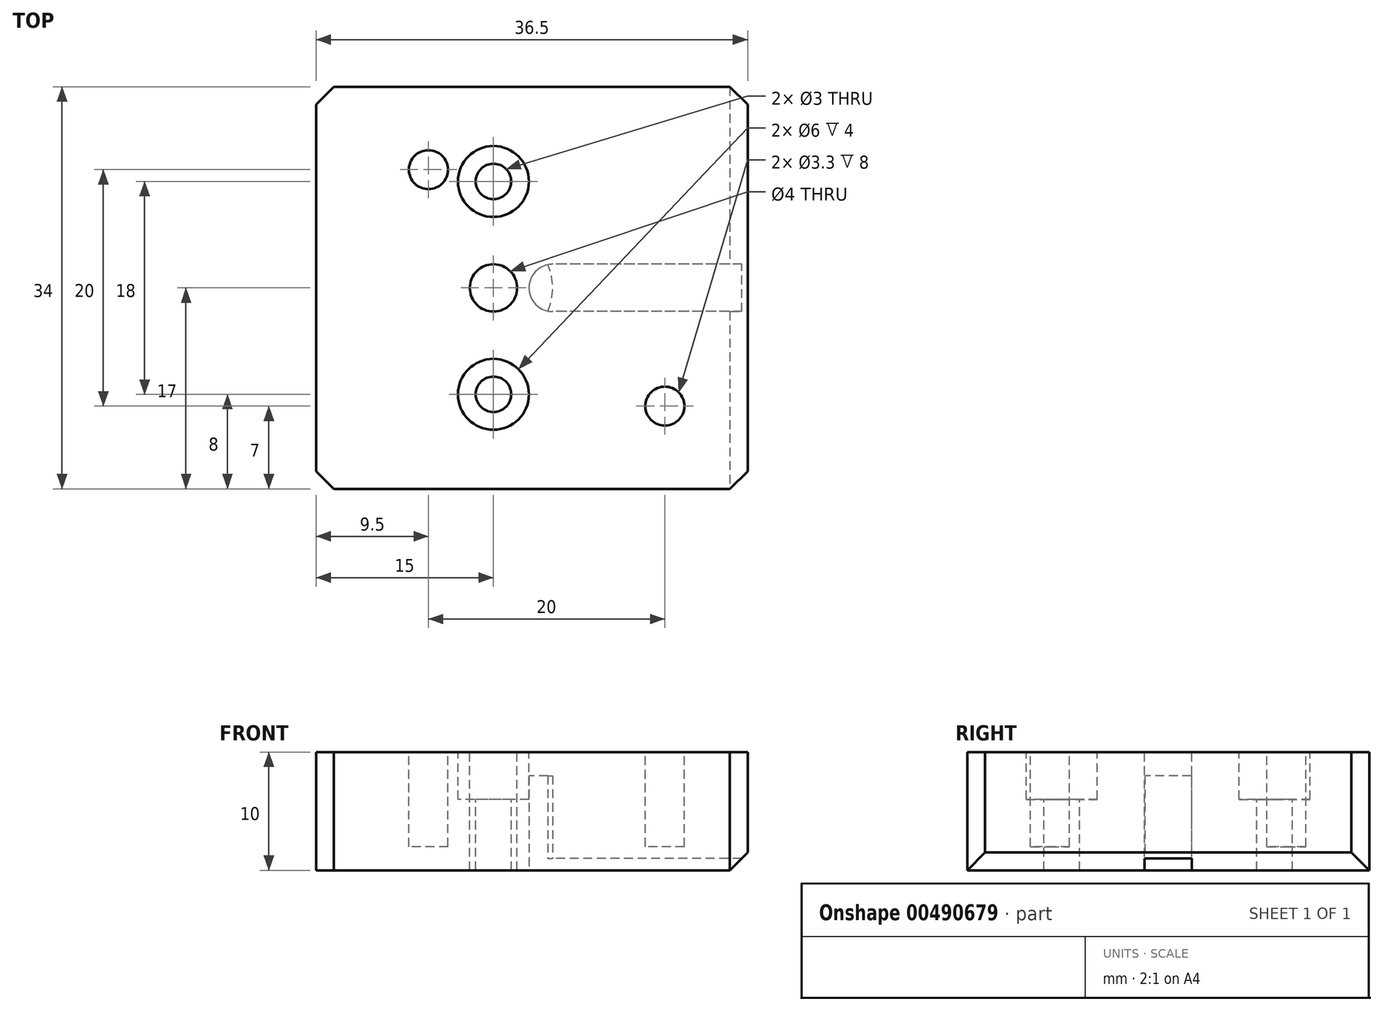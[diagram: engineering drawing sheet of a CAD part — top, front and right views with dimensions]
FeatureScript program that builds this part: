
annotation { "Feature Type Name" : "Feature", "Feature Type Description" : "" }
export const myFeature = defineFeature(function(context is Context, id is Id, definition is map)
    precondition{}
    {
        {
            var Q0;
            Q0=qCreatedBy(makeId("Top.planeOp"),FACE);
            var sketch = newSketch(context, id + "F0", { "sketchPlane" : qUnion([Q0])});
            skLineSegment(sketch, "E0.bottom", {"start": v(0, 0) * mm, "end": v(30, 0) * mm});
            skLineSegment(sketch, "E0.top", {"start": v(0, -30) * mm, "end": v(30, -30) * mm});
            skLineSegment(sketch, "E0.left", {"start": v(0, 0) * mm, "end": v(0, -30) * mm});
            skLineSegment(sketch, "E0.right", {"start": v(30, 0) * mm, "end": v(30, -30) * mm});
            skLineSegment(sketch, "E1", {"start": v(0, -15) * mm, "end": v(30, -15) * mm, "construction": true});
            skCircle(sketch, "E2", {"center": v(15, -15) * mm, "radius": 2 * mm});
            skLineSegment(sketch, "E3", {"start": v(0, -5) * mm, "end": v(9.5, -5) * mm, "construction": true});
            skLineSegment(sketch, "E4", {"start": v(9.5, -5) * mm, "end": v(9.5, 0) * mm, "construction": true});
            skCircle(sketch, "E5", {"center": v(9.5, -5) * mm, "radius": 1.65 * mm});
            skCircle(sketch, "E6.0.1.0", {"center": v(9.5, -25) * mm, "radius": 1.65 * mm, "construction": true});
            skLineSegment(sketch, "E6.direction2", {"start": v(9.5, -5) * mm, "end": v(9.5, -25) * mm, "construction": true});
            skLineSegment(sketch, "E7", {"start": v(15, -30) * mm, "end": v(15, 0) * mm, "construction": true});
            skCircle(sketch, "E8", {"center": v(15, -6) * mm, "radius": 1.5 * mm});
            skCircle(sketch, "E9", {"center": v(15, -24) * mm, "radius": 1.5 * mm});
            skCircle(sketch, "E10", {"center": v(15, -6) * mm, "radius": 3 * mm});
            skCircle(sketch, "E11", {"center": v(15, -24) * mm, "radius": 3 * mm});
            skCircle(sketch, "E12", {"center": v(6, -15) * mm, "radius": 1.5 * mm});
            skCircle(sketch, "E13", {"center": v(6, -15) * mm, "radius": 3 * mm});
            skCircle(sketch, "E14", {"center": v(24, -15) * mm, "radius": 3 * mm});
            skCircle(sketch, "E15", {"center": v(24, -15) * mm, "radius": 1.5 * mm});
            skSolve(sketch);
        }
        {
            var Q0;
            Q0=makeQuery(id+"F0.imprint","IMPRINT",FACE,{"disambiguationData":[TD([[makeQuery(id+"F0.imprint","IMPRINT",EDGE,{"derivedFrom":sQuery(id+"F0.wireOp",EDGE,"E0.bottom")}),-1.0]])]});
            var Q1;
            Q1=makeQuery(id+"F0.imprint","IMPRINT",FACE,{"disambiguationData":[TD([[makeQuery(id+"F0.imprint","IMPRINT",EDGE,{"derivedFrom":sQuery(id+"F0.wireOp",EDGE,"E2")}),1.0]])]});
            var Q2;
            Q2=makeQuery(id+"F0.imprint","IMPRINT",FACE,{"disambiguationData":[TD([[makeQuery(id+"F0.imprint","IMPRINT",EDGE,{"derivedFrom":sQuery(id+"F0.wireOp",EDGE,"E8")}),-1.0]])]});
            var Q3;
            Q3=makeQuery(id+"F0.imprint","IMPRINT",FACE,{"disambiguationData":[TD([[makeQuery(id+"F0.imprint","IMPRINT",EDGE,{"derivedFrom":sQuery(id+"F0.wireOp",EDGE,"E9")}),-1.0]])]});
            var Q4;
            Q4=makeQuery(id+"F0.imprint","IMPRINT",FACE,{"disambiguationData":[TD([[makeQuery(id+"F0.imprint","IMPRINT",EDGE,{"derivedFrom":sQuery(id+"F0.wireOp",EDGE,"E5")}),1.0]])]});
            var Q5;
            Q5=makeQuery(id+"F0.imprint","IMPRINT",FACE,{"disambiguationData":[TD([[makeQuery(id+"F0.imprint","IMPRINT",EDGE,{"derivedFrom":sQuery(id+"F0.wireOp",EDGE,"E6.0.1.0")}),1.0]])]});
            var Q6;
            Q6=makeQuery(id+"F0.imprint","IMPRINT",FACE,{"disambiguationData":[TD([[makeQuery(id+"F0.imprint","IMPRINT",EDGE,{"derivedFrom":sQuery(id+"F0.wireOp",EDGE,"E14")}),1.0]])]});
            var Q7;
            Q7=makeQuery(id+"F0.imprint","IMPRINT",FACE,{"disambiguationData":[TD([[makeQuery(id+"F0.imprint","IMPRINT",EDGE,{"derivedFrom":sQuery(id+"F0.wireOp",EDGE,"E12")}),-1.0]])]});
            var Q8;
            Q8=makeQuery(id+"F0.imprint","IMPRINT",FACE,{"disambiguationData":[TD([[makeQuery(id+"F0.imprint","IMPRINT",EDGE,{"derivedFrom":sQuery(id+"F0.wireOp",EDGE,"E12")}),1.0]])]});
            var Q9;
            Q9=makeQuery(id+"F0.imprint","IMPRINT",FACE,{"disambiguationData":[TD([[makeQuery(id+"F0.imprint","IMPRINT",EDGE,{"derivedFrom":sQuery(id+"F0.wireOp",EDGE,"E15")}),1.0]])]});
            extrude(context, id + "F1", {"entities" : qUnion([Q0, Q1, Q2, Q3, Q4, Q5, Q6, Q7, Q8, Q9]), "oppositeDirection" : true, "depth" : 10 * mm, "offsetDistance" : 25 * mm});
        }
        {
            var Q0;
            Q0=makeQuery(id+"F0.imprint","IMPRINT",FACE,{"disambiguationData":[TD([[makeQuery(id+"F0.imprint","IMPRINT",EDGE,{"derivedFrom":sQuery(id+"F0.wireOp",EDGE,"CrWIfdQ6-x99r-vkrS-wa22-O8fHmD59tpvO")}),1.0]])]});
            var Q1;
            Q1=makeQuery(id+"F0.imprint","IMPRINT",FACE,{"disambiguationData":[TD([[makeQuery(id+"F0.imprint","IMPRINT",EDGE,{"derivedFrom":sQuery(id+"F0.wireOp",EDGE,"E2")}),1.0]])]});
            extrude(context, id + "F2", {"entities" : qUnion([Q0, Q1]), "operationType" : NewBodyOperationType.REMOVE, "oppositeDirection" : true, "depth" : 12 * mm, "offsetDistance" : 25 * mm});
        }
        {
            var Q0;
            Q0=makeQuery(id+"F0.imprint","IMPRINT",FACE,{"disambiguationData":[TD([[makeQuery(id+"F0.imprint","IMPRINT",EDGE,{"derivedFrom":sQuery(id+"F0.wireOp",EDGE,"E9")}),-1.0]])]});
            var Q1;
            Q1=makeQuery(id+"F0.imprint","IMPRINT",FACE,{"disambiguationData":[TD([[makeQuery(id+"F0.imprint","IMPRINT",EDGE,{"derivedFrom":sQuery(id+"F0.wireOp",EDGE,"E8")}),-1.0]])]});
            extrude(context, id + "F3", {"entities" : qUnion([Q0, Q1]), "operationType" : NewBodyOperationType.REMOVE, "oppositeDirection" : true, "depth" : 4 * mm, "offsetDistance" : 25 * mm});
        }
        {
            var Q0;
            Q0=makeQuery(id+"F1.opExtrude","CAP_FACE",FACE,{"disambiguationData":[OSD([sQuery(id+"F0.wireOp",EDGE,"E0.bottom"),sQuery(id+"F0.wireOp",EDGE,"E0.top"),sQuery(id+"F0.wireOp",EDGE,"E0.left"),sQuery(id+"F0.wireOp",EDGE,"E0.right"),sQuery(id+"F0.wireOp",EDGE,"E8"),sQuery(id+"F0.wireOp",EDGE,"E9")])],"isStart":false});
            var sketch = newSketch(context, id + "F4", { "sketchPlane" : qUnion([Q0])});
            skCircle(sketch, "E16", {"center": v(15, 15) * mm, "radius": 5 * mm});
            skLineSegment(sketch, "E17", {"start": v(30, 15) * mm, "end": v(20, 15) * mm, "construction": true});
            skArc(sketch, "E18.0.startCap", {"start": v(30, 17) * mm, "mid": v(32, 15) * mm, "end": v(30, 13) * mm});
            skArc(sketch, "E18.0.endCap", {"start": v(20, 13) * mm, "mid": v(18, 15) * mm, "end": v(20, 17) * mm});
            skLineSegment(sketch, "E18.0.left", {"start": v(30, 13) * mm, "end": v(20, 13) * mm});
            skLineSegment(sketch, "E18.0.right", {"start": v(30, 17) * mm, "end": v(20, 17) * mm});
            skLineSegment(sketch, "E19", {"start": v(3.5, 0) * mm, "end": v(3.5, 3.5) * mm, "construction": true});
            skLineSegment(sketch, "E20", {"start": v(3.5, 3.5) * mm, "end": v(0, 3.5) * mm, "construction": true});
            skCircle(sketch, "E21", {"center": v(3.5, 3.5) * mm, "radius": 1.25 * mm});
            skCircle(sketch, "E22", {"center": v(3.5, 3.5) * mm, "radius": 2.5 * mm});
            skCircle(sketch, "E23.0.1.0", {"center": v(3.5, 26.5) * mm, "radius": 1.25 * mm});
            skCircle(sketch, "E23.0.1.1", {"center": v(3.5, 26.5) * mm, "radius": 2.5 * mm});
            skCircle(sketch, "E23.1.0.0", {"center": v(26.5, 3.5) * mm, "radius": 1.25 * mm});
            skCircle(sketch, "E23.1.0.1", {"center": v(26.5, 3.5) * mm, "radius": 2.5 * mm});
            skCircle(sketch, "E23.1.1.0", {"center": v(26.5, 26.5) * mm, "radius": 1.25 * mm});
            skCircle(sketch, "E23.1.1.1", {"center": v(26.5, 26.5) * mm, "radius": 2.5 * mm});
            skLineSegment(sketch, "E23.direction1", {"start": v(3.5, 3.5) * mm, "end": v(26.5, 3.5) * mm, "construction": true});
            skLineSegment(sketch, "E23.direction2", {"start": v(3.5, 3.5) * mm, "end": v(3.5, 26.5) * mm, "construction": true});
            skSolve(sketch);
        }
        {
            var Q0;
            Q0=makeQuery(id+"F4.imprint","IMPRINT",FACE,{"disambiguationData":[TD([[makeQuery(id+"F4.imprint","IMPRINT",EDGE,{"derivedFrom":sQuery(id+"F4.wireOp",EDGE,"E16")}),1.0]])]});
            var Q1;
            {var subQ0=sQuery(id+"F4.wireOp",EDGE,"E18.0.endCap");var subQ1=sQuery(id+"F4.wireOp",EDGE,"E16");var subQ2=makeQuery(id+"F4.imprint","INTERSECT",VERTEX,{"disambiguationData":[OD(0.0)],"derivedFrom":[subQ1,subQ0]});Q1=makeQuery(id+"F4.imprint","IMPRINT",FACE,{"disambiguationData":[TD([[makeQuery(id+"F4.imprint","IMPRINT",EDGE,{"disambiguationData":[TD([[subQ2,1.0]])],"derivedFrom":subQ1}),1.0]])]});}
            extrude(context, id + "F5", {"entities" : qUnion([Q0, Q1]), "operationType" : NewBodyOperationType.REMOVE, "oppositeDirection" : true, "depth" : 8 * mm, "offsetDistance" : 25 * mm});
        }
        {
            var Q0;
            {var subQ4=sQuery(id+"F4.wireOp",EDGE,"E18.0.left");Q0=makeQuery(id+"F4.imprint","IMPRINT",FACE,{"disambiguationData":[TD([[makeQuery(id+"F4.imprint","IMPRINT",EDGE,{"derivedFrom":subQ4}),-1.0]])]});}
            extrude(context, id + "F6", {"entities" : qUnion([Q0]), "operationType" : NewBodyOperationType.REMOVE, "oppositeDirection" : true, "depth" : 1 * mm, "offsetDistance" : 25 * mm});
        }
        {
            var Q0;
            Q0=makeQuery(id+"F1.opExtrude","SWEPT_FACE",FACE,{"disambiguationData":[OSD([sQuery(id+"F0.wireOp",EDGE,"E0.right")])]});
            extrude(context, id + "F7", {"entities" : qUnion([Q0]), "operationType" : NewBodyOperationType.ADD, "depth" : 4.5 * mm, "offsetDistance" : 25 * mm});
        }
        {
            var Q0;
            {var subQ0=sQuery(id+"F0.wireOp",EDGE,"E0.bottom");Q0=makeQuery(id+"F7.boolean.opBoolean","MERGE",FACE,{"derivedFrom":[makeQuery(id+"F1.opExtrude","SWEPT_FACE",FACE,{"disambiguationData":[OSD([subQ0])]}),makeQuery(id+"F7.opExtrude","SWEPT_FACE",FACE,{"disambiguationData":[OSD([subQ0,sQuery(id+"F0.wireOp",EDGE,"E0.right")])]})]});}
            extrude(context, id + "F8", {"entities" : qUnion([Q0]), "operationType" : NewBodyOperationType.ADD, "depth" : 2 * mm, "offsetDistance" : 25 * mm});
        }
        {
            var Q0;
            {var subQ0=sQuery(id+"F0.wireOp",EDGE,"E0.top");Q0=makeQuery(id+"F7.boolean.opBoolean","MERGE",FACE,{"derivedFrom":[makeQuery(id+"F1.opExtrude","SWEPT_FACE",FACE,{"disambiguationData":[OSD([subQ0])]}),makeQuery(id+"F7.opExtrude","SWEPT_FACE",FACE,{"disambiguationData":[OSD([subQ0,sQuery(id+"F0.wireOp",EDGE,"E0.right")])]})]});}
            extrude(context, id + "F9", {"entities" : qUnion([Q0]), "operationType" : NewBodyOperationType.ADD, "depth" : 2 * mm, "offsetDistance" : 25 * mm});
        }
        {
            var Q0;
            {var subQ0=sQuery(id+"F0.wireOp",EDGE,"E0.right");var subQ1=sQuery(id+"F0.wireOp",EDGE,"E0.top");var subQ2=sQuery(id+"F0.wireOp",EDGE,"E0.bottom");Q0=makeQuery(id+"F9.boolean.opBoolean","MERGE",FACE,{"derivedFrom":[makeQuery(id+"F8.boolean.opBoolean","MERGE",FACE,{"derivedFrom":[makeQuery(id+"F7.opExtrude","CAP_FACE",FACE,{"disambiguationData":[OSD([subQ0])],"isStart":false}),makeQuery(id+"F8.opExtrude","SWEPT_FACE",FACE,{"disambiguationData":[OSD([subQ2,subQ0]),TDD([makeQuery(id+"F7.opExtrude","CAP_EDGE",EDGE,{"disambiguationData":[OSD([subQ2,subQ0])],"isStart":false})])]})]}),makeQuery(id+"F9.opExtrude","SWEPT_FACE",FACE,{"disambiguationData":[OSD([subQ1,subQ0]),TDD([makeQuery(id+"F7.opExtrude","CAP_EDGE",EDGE,{"disambiguationData":[OSD([subQ1,subQ0])],"isStart":false})])]})]});}
            extrude(context, id + "F10", {"entities" : qUnion([Q0]), "operationType" : NewBodyOperationType.ADD, "depth" : 2 * mm, "offsetDistance" : 25 * mm});
        }
        {
            var Q0;
            Q0=makeQuery(id+"F1.opExtrude","SWEPT_EDGE",EDGE,{"disambiguationData":[OSD([sQuery(id+"F0.wireOp",EDGE,"E0.top"),sQuery(id+"F0.wireOp",EDGE,"E0.right")])]});
            var Q1;
            Q1=makeQuery(id+"F1.opExtrude","SWEPT_EDGE",EDGE,{"disambiguationData":[OSD([sQuery(id+"F0.wireOp",EDGE,"E0.top"),sQuery(id+"F0.wireOp",EDGE,"E0.left")])]});
            var Q2;
            Q2=makeQuery(id+"F1.opExtrude","SWEPT_EDGE",EDGE,{"disambiguationData":[OSD([sQuery(id+"F0.wireOp",EDGE,"E0.bottom"),sQuery(id+"F0.wireOp",EDGE,"E0.left")])]});
            var Q3;
            Q3=makeQuery(id+"F1.opExtrude","SWEPT_EDGE",EDGE,{"disambiguationData":[OSD([sQuery(id+"F0.wireOp",EDGE,"E0.bottom"),sQuery(id+"F0.wireOp",EDGE,"E0.right")])]});
            var Q4;
            Q4=makeQuery(id+"F7.boolean.opBoolean","COPY",EDGE,{"derivedFrom":makeQuery(id+"F7.opExtrude","CAP_EDGE",EDGE,{"disambiguationData":[OSD([sQuery(id+"F0.wireOp",EDGE,"E0.top"),sQuery(id+"F0.wireOp",EDGE,"E0.right")])],"isStart":false})});
            var Q5;
            Q5=makeQuery(id+"F7.boolean.opBoolean","COPY",EDGE,{"derivedFrom":makeQuery(id+"F7.opExtrude","CAP_EDGE",EDGE,{"disambiguationData":[OSD([sQuery(id+"F0.wireOp",EDGE,"E0.bottom"),sQuery(id+"F0.wireOp",EDGE,"E0.right")])],"isStart":false})});
            var Q6;
            Q6=makeQuery(id+"F7.opExtrude","CAP_EDGE",EDGE,{"disambiguationData":[OSD([sQuery(id+"F0.wireOp",EDGE,"E0.top"),sQuery(id+"F0.wireOp",EDGE,"E0.right")])],"isStart":false});
            var Q7;
            Q7=makeQuery(id+"F7.opExtrude","CAP_EDGE",EDGE,{"disambiguationData":[OSD([sQuery(id+"F0.wireOp",EDGE,"E0.bottom"),sQuery(id+"F0.wireOp",EDGE,"E0.right")])],"isStart":false});
            var Q8;
            Q8=makeQuery(id+"F9.opExtrude","CAP_EDGE",EDGE,{"disambiguationData":[OSD([sQuery(id+"F0.wireOp",EDGE,"E0.top"),sQuery(id+"F0.wireOp",EDGE,"E0.left")])],"isStart":false});
            var Q9;
            Q9=makeQuery(id+"F8.opExtrude","CAP_EDGE",EDGE,{"disambiguationData":[OSD([sQuery(id+"F0.wireOp",EDGE,"E0.bottom"),sQuery(id+"F0.wireOp",EDGE,"E0.left")])],"isStart":false});
            var Q10;
            {var subQ0=sQuery(id+"F0.wireOp",EDGE,"E0.right");var subQ1=sQuery(id+"F0.wireOp",EDGE,"E0.top");Q10=makeQuery(id+"F9.opExtrude","CAP_EDGE",EDGE,{"disambiguationData":[OSD([subQ1,subQ0]),TDD([makeQuery(id+"F7.opExtrude","CAP_EDGE",EDGE,{"disambiguationData":[OSD([subQ1,subQ0])],"isStart":false})])],"isStart":false});}
            var Q11;
            {var subQ0=sQuery(id+"F0.wireOp",EDGE,"E0.right");var subQ1=sQuery(id+"F0.wireOp",EDGE,"E0.bottom");Q11=makeQuery(id+"F8.opExtrude","CAP_EDGE",EDGE,{"disambiguationData":[OSD([subQ1,subQ0]),TDD([makeQuery(id+"F7.opExtrude","CAP_EDGE",EDGE,{"disambiguationData":[OSD([subQ1,subQ0])],"isStart":false})])],"isStart":false});}
            var Q12;
            Q12=makeQuery(id+"F10.opExtrude","CAP_EDGE",EDGE,{"disambiguationData":[OSD([sQuery(id+"F0.wireOp",EDGE,"E0.top"),sQuery(id+"F0.wireOp",EDGE,"E0.left")])],"isStart":false});
            var Q13;
            Q13=makeQuery(id+"F10.opExtrude","CAP_EDGE",EDGE,{"disambiguationData":[OSD([sQuery(id+"F0.wireOp",EDGE,"E0.bottom"),sQuery(id+"F0.wireOp",EDGE,"E0.left")])],"isStart":false});
            chamfer(context, id + "F11", {"entities" : qUnion([Q0, Q1, Q2, Q3, Q4, Q5, Q6, Q7, Q8, Q9, Q10, Q11, Q12, Q13]), "width" : 1.5 * mm, "tangentPropagation" : true});
        }
        {
            var Q0;
            {var subQ0=sQuery(id+"F0.wireOp",EDGE,"E0.right");var subQ1=sQuery(id+"F0.wireOp",EDGE,"E0.top");var subQ2=sQuery(id+"F0.wireOp",EDGE,"E0.bottom");Q0=makeQuery(id+"F10.boolean.opBoolean","MERGE",FACE,{"derivedFrom":[makeQuery(id+"F9.boolean.opBoolean","MERGE",FACE,{"derivedFrom":[makeQuery(id+"F8.boolean.opBoolean","MERGE",FACE,{"derivedFrom":[makeQuery(id+"F7.boolean.opBoolean","MERGE",FACE,{"derivedFrom":[makeQuery(id+"F1.opExtrude","CAP_FACE",FACE,{"disambiguationData":[OSD([subQ2,subQ1,sQuery(id+"F0.wireOp",EDGE,"E0.left"),subQ0,sQuery(id+"F0.wireOp",EDGE,"E8"),sQuery(id+"F0.wireOp",EDGE,"E9")])],"isStart":true}),makeQuery(id+"F7.opExtrude","SWEPT_FACE",FACE,{"disambiguationData":[OSD([subQ0]),TDD([makeQuery(id+"F1.opExtrude","CAP_EDGE",EDGE,{"disambiguationData":[OSD([subQ0])],"isStart":true})])]})]}),makeQuery(id+"F8.opExtrude","SWEPT_FACE",FACE,{"disambiguationData":[OSD([subQ2,subQ0]),TDD([makeQuery(id+"F7.boolean.opBoolean","MERGE",EDGE,{"derivedFrom":[makeQuery(id+"F1.opExtrude","CAP_EDGE",EDGE,{"disambiguationData":[OSD([subQ2])],"isStart":true}),makeQuery(id+"F7.opExtrude","SWEPT_EDGE",EDGE,{"disambiguationData":[OSD([subQ2,subQ0]),TDD([makeQuery(id+"F1.opExtrude","CAP_VERTEX",VERTEX,{"disambiguationData":[OSD([subQ2,subQ0])],"isStart":true})])]})]})])]})]}),makeQuery(id+"F9.opExtrude","SWEPT_FACE",FACE,{"disambiguationData":[OSD([subQ1,subQ0]),TDD([makeQuery(id+"F7.boolean.opBoolean","MERGE",EDGE,{"derivedFrom":[makeQuery(id+"F1.opExtrude","CAP_EDGE",EDGE,{"disambiguationData":[OSD([subQ1])],"isStart":true}),makeQuery(id+"F7.opExtrude","SWEPT_EDGE",EDGE,{"disambiguationData":[OSD([subQ1,subQ0]),TDD([makeQuery(id+"F1.opExtrude","CAP_VERTEX",VERTEX,{"disambiguationData":[OSD([subQ1,subQ0])],"isStart":true})])]})]})])]})]}),makeQuery(id+"F10.opExtrude","SWEPT_FACE",FACE,{"disambiguationData":[OSD([subQ2,subQ1,subQ0])]})]});}
            var sketch = newSketch(context, id + "F12", { "sketchPlane" : qUnion([Q0])});
            skCircle(sketch, "E24", {"center": v(29.5, -25) * mm, "radius": 1.65 * mm});
            skSolve(sketch);
        }
        {
            var Q0;
            Q0=makeQuery(id+"F0.imprint","IMPRINT",FACE,{"disambiguationData":[TD([[makeQuery(id+"F0.imprint","IMPRINT",EDGE,{"derivedFrom":sQuery(id+"F0.wireOp",EDGE,"E5")}),1.0]])]});
            var Q1;
            Q1=makeQuery(id+"F12.imprint","IMPRINT",FACE,{"disambiguationData":[TD([[makeQuery(id+"F12.imprint","IMPRINT",EDGE,{"derivedFrom":sQuery(id+"F12.wireOp",EDGE,"E24")}),1.0]])]});
            extrude(context, id + "F13", {"entities" : qUnion([Q0, Q1]), "operationType" : NewBodyOperationType.REMOVE, "oppositeDirection" : true, "depth" : 8 * mm, "offsetDistance" : 25 * mm});
        }
    });
